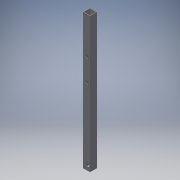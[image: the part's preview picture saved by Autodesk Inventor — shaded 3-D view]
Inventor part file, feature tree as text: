
AUTODESK INVENTOR PART (.ipt)
format: ipt  version: 2016 (Build 200138000, 138)  size: 145,408 bytes
history: native  units: in
note: dims shown in document units (in); Inventor stores cm internally (conversion verified against a paired STEP export)
features: extrude x6, sketch x6
ambient origin geometry x8: Origin, YZ Plane, XZ Plane, XY Plane, X Axis, Y Axis, Z Axis, Center Point
bodies: Solid1 (feature_tree)
feature tree (12):
  extrude  "Extrusion1"  Depth=1.0in
  extrude  "Extrusion3"  Depth=0.0625in TaperAngle=0.0deg
  extrude  "Extrusion4"  Depth=7.0in
  extrude  "Extrusion5"  Depth=1.0in
  extrude  "Extrusion6"  Depth=8.6in
  extrude  "Extrusion7"  Depth=1.0in
  sketch  "Sketch1"  dims[d0=1.0in d1=1.0in]
  sketch  "Sketch3"  dims[d2=0.0625in d3=18.0in d4=0.0in]
  sketch  "Sketch4"  dims[d9=0.5in d10=7.0in]
  sketch  "Sketch5"  dims[d11=1.0in d12=0.0in d13=0.5in]
  sketch  "Sketch6"  dims[d14=0.53in d15=8.6in]
  sketch  "Sketch7"  dims[d16=1.0in d17=0.0in d18=0.555in d19=1.5in d20=0.0in d21=0.5in d22=1.745in d23=0.646in d24=1.5in d25=0.0in d26=0.5in d27=0.4666in d28=16.568in d29=1.0in d30=0.0in]
